SOLIDWORKS PART (.sldprt)
format: sldprt  version: not decoded by parser v0  size: 58,880 bytes
history: native  units: mm
features: sketch x3, fillet x2, cut_extrude x2, extrude x1, pattern_linear x1 + 2 further entries (+9 scaffold rows collapsed; 3 parser-record rows omitted)
feature tree (23):
  scaffold x9  (default folders/planes/origin — collapsed)
  parser-record x3  (decoder bookkeeping rows leaked as tree rows — omitted from the tree; the rows remain in map.json)
  "ID2"
  "ID3"
  sketch  "Sketch1"  dims[D1=38.1mm D2=6.35mm]
  extrude  "Extrude1"  Depth=147.574mm
  fillet  "Fillet1"  Radius=6.35mm
  fillet  "Fillet2"  Radius=7.9248mm
  sketch  "Sketch2"  dims[D1=8.3312mm D2=16.637mm]
  cut_extrude  "Cut-Extrude1"  [1 undecoded]
  sketch  "Sketch3"  dims[D1=8.3312mm D2=16.637mm]
  cut_extrude  "Cut-Extrude2"  [1 undecoded]
  pattern_linear  "LPattern1"  Count1=4 Count2=1 Spacing1=38.1mm Spacing2=50mm
decode coverage: 7 of 9 modeling features carry decoded parameters; 2 rows unclassified (native names shown)
note: 2 parameter values undecoded
note: suppression state not decoded; provenance and decode notes live in map.json
